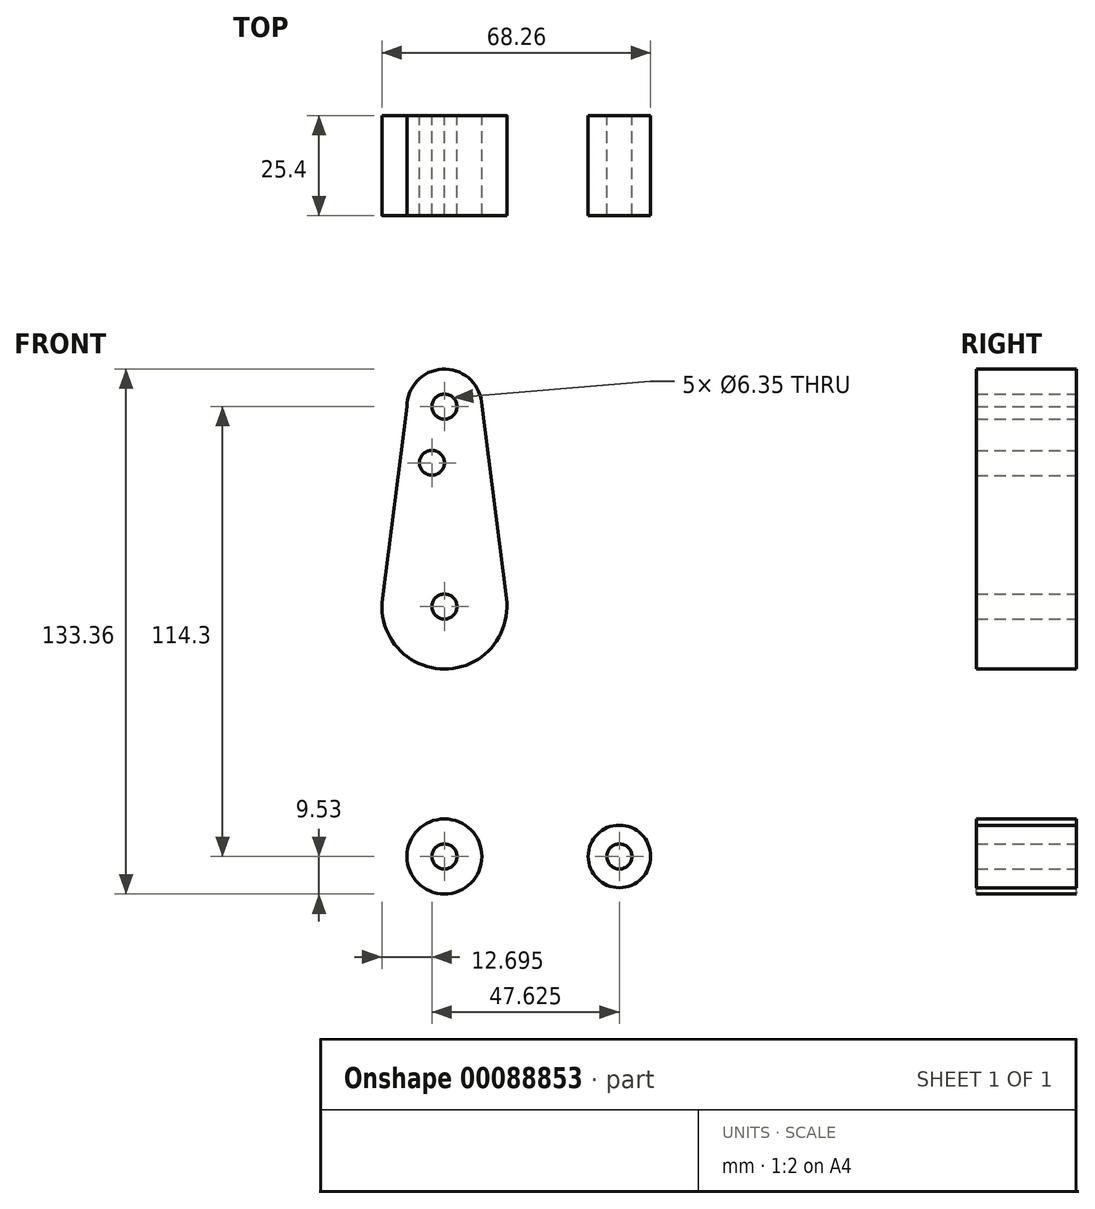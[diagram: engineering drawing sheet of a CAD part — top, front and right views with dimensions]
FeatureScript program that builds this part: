
annotation { "Feature Type Name" : "Feature", "Feature Type Description" : "" }
export const myFeature = defineFeature(function(context is Context, id is Id, definition is map)
    precondition{}
    {
        {
            var Q0;
            Q0=qCreatedBy(makeId("Front.planeOp"),FACE);
            var sketch = newSketch(context, id + "F0", { "sketchPlane" : qUnion([Q0])});
            skLineSegment(sketch, "E0", {"start": v(0, 114.3) * mm, "end": v(0, 0) * mm, "construction": true});
            skLineSegment(sketch, "E1", {"start": v(0, 0) * mm, "end": v(44.45, 0) * mm, "construction": true});
            skCircle(sketch, "E2", {"center": v(0, 114.3) * mm, "radius": 9.53 * mm});
            skCircle(sketch, "E3", {"center": v(0, 63.5) * mm, "radius": 15.88 * mm});
            skPoint(sketch, "E4", {"position": v(9.53, 0) * mm});
            skPoint(sketch, "E5", {"position": v(0, -41.04) * mm});
            skPoint(sketch, "E6", {"position": v(-9.57, 0) * mm});
            skPoint(sketch, "E7", {"position": v(0, -9.52) * mm});
            skPoint(sketch, "E8", {"position": v(-9.53, 114.3) * mm});
            skPoint(sketch, "E9", {"position": v(9.45, 115.5) * mm});
            skPoint(sketch, "E10", {"position": v(44.52, 7.94) * mm});
            skPoint(sketch, "E11", {"position": v(44.73, -7.93) * mm});
            skLineSegment(sketch, "E12", {"start": v(18.71, 8.15) * mm, "end": v(44.52, 7.94) * mm});
            skLineSegment(sketch, "E13", {"start": v(0, -9.53) * mm, "end": v(44.73, -7.93) * mm});
            skLineSegment(sketch, "E14", {"start": v(-9.53, 114.3) * mm, "end": v(-15.75, 65.5) * mm});
            skLineSegment(sketch, "E15", {"start": v(9.45, 115.5) * mm, "end": v(15.75, 65.48) * mm});
            skLineSegment(sketch, "E16", {"start": v(-15.8, 61.91) * mm, "end": v(-9.57, 0) * mm});
            skLineSegment(sketch, "E17", {"start": v(15.78, 61.77) * mm, "end": v(10.88, 16.97) * mm});
            skCircle(sketch, "E18", {"center": v(-3.18, 100.03) * mm, "radius": 3.18 * mm});
            skCircle(sketch, "E19", {"center": v(0, 63.5) * mm, "radius": 3.18 * mm});
            skCircle(sketch, "E20", {"center": v(0, 114.3) * mm, "radius": 3.18 * mm});
            skCircle(sketch, "E21", {"center": v(0, 0) * mm, "radius": 3.18 * mm});
            skCircle(sketch, "E22", {"center": v(44.45, 0) * mm, "radius": 3.18 * mm});
            skArc(sketch, "E23.filletArc", {"start": v(10.88, 16.97) * mm, "mid": v(12.84, 10.82) * mm, "end": v(18.71, 8.15) * mm});
            skCircle(sketch, "E24", {"center": v(0, 0) * mm, "radius": 9.52 * mm});
            skCircle(sketch, "E25", {"center": v(44.45, 0) * mm, "radius": 7.94 * mm});
            skSolve(sketch);
        }
        {
            var Q0;
            Q0 = qSketchRegion(id + "F0", true);
            extrude(context, id + "F1", {"entities" : qUnion([Q0]), "depth" : 25.4 * mm});
        }
    });
